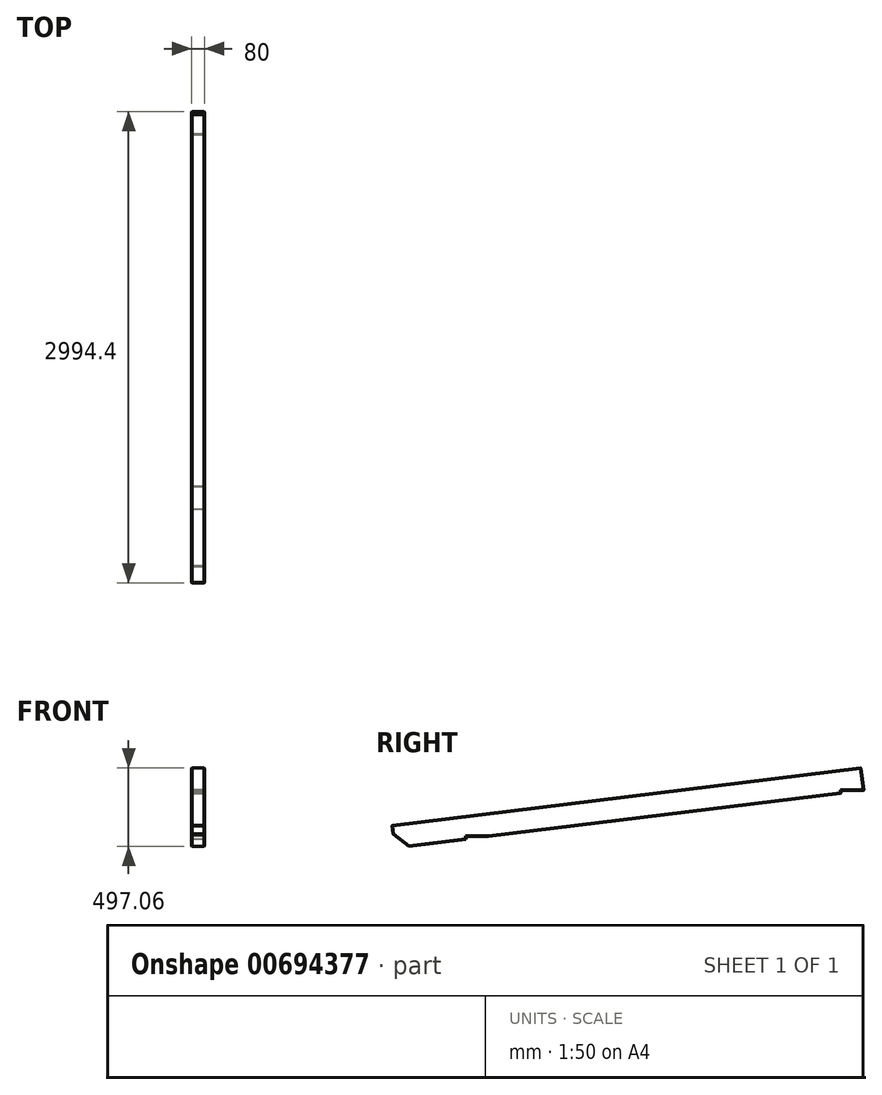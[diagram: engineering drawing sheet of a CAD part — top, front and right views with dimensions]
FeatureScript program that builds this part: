
annotation { "Feature Type Name" : "Feature", "Feature Type Description" : "" }
export const myFeature = defineFeature(function(context is Context, id is Id, definition is map)
    precondition{}
    {
        {
            var Q0;
            Q0=qCreatedBy(makeId("Right.planeOp"),FACE);
            var sketch = newSketch(context, id + "F0", { "sketchPlane" : qUnion([Q0])});
            skLineSegment(sketch, "E0.trimOffspring", {"start": v(2426.65, 153.57) * mm, "end": v(2426.66, 153.57) * mm, "construction": true});
            skLineSegment(sketch, "E1.right", {"start": v(44.48, -138.84) * mm, "end": v(44.48, -138.92) * mm, "construction": true});
            skLineSegment(sketch, "E2", {"start": v(-568.53, -69.1) * mm, "end": v(-561.93, -122.85) * mm});
            skLineSegment(sketch, "E3", {"start": v(-561.93, -122.85) * mm, "end": v(-461.8, -201.08) * mm});
            skLineSegment(sketch, "E4", {"start": v(-461.8, -201.08) * mm, "end": v(-99.52, -156.6) * mm});
            skLineSegment(sketch, "E5", {"start": v(-99.52, -156.6) * mm, "end": v(-99.52, -138.84) * mm});
            skLineSegment(sketch, "E6", {"start": v(-99.52, -138.84) * mm, "end": v(44.48, -138.84) * mm});
            skLineSegment(sketch, "E7", {"start": v(44.48, -138.84) * mm, "end": v(2282.47, 135.87) * mm});
            skLineSegment(sketch, "E8", {"start": v(2282.47, 135.87) * mm, "end": v(2282.47, 153.57) * mm});
            skLineSegment(sketch, "E9", {"start": v(2282.47, 153.57) * mm, "end": v(2426.66, 153.57) * mm});
            skLineSegment(sketch, "E10", {"start": v(2426.66, 153.57) * mm, "end": v(2409.1, 296.5) * mm});
            skLineSegment(sketch, "E11", {"start": v(2409.1, 296.5) * mm, "end": v(-568.53, -69.1) * mm});
            skSolve(sketch);
        }
        {
            var Q0;
            Q0=makeQuery(id+"F0.imprint","IMPRINT",FACE,{"disambiguationData":[TD([[makeQuery(id+"F0.imprint","IMPRINT",EDGE,{"derivedFrom":sQuery(id+"F0.wireOp",EDGE,"E2")}),1.0]])]});
            extrude(context, id + "F1", {"entities" : qUnion([Q0]), "depth" : 80 * mm, "offsetDistance" : 25 * mm});
        }
        {
            var Q0;
            Q0=makeQuery(id+"F1.opExtrude","SWEPT_FACE",FACE,{"disambiguationData":[OSD([sQuery(id+"F0.wireOp",EDGE,"E2")])]});
            var Q1;
            Q1=makeQuery(id+"F1.opExtrude","SWEPT_FACE",FACE,{"disambiguationData":[OSD([sQuery(id+"F0.wireOp",EDGE,"E3")])]});
            var Q2;
            Q2=makeQuery(id+"F1.opExtrude","CAP_FACE",FACE,{"disambiguationData":[OSD([sQuery(id+"F0.wireOp",EDGE,"E2"),sQuery(id+"F0.wireOp",EDGE,"E3"),sQuery(id+"F0.wireOp",EDGE,"E4"),sQuery(id+"F0.wireOp",EDGE,"E5"),sQuery(id+"F0.wireOp",EDGE,"E6"),sQuery(id+"F0.wireOp",EDGE,"E7"),sQuery(id+"F0.wireOp",EDGE,"E8"),sQuery(id+"F0.wireOp",EDGE,"E9"),sQuery(id+"F0.wireOp",EDGE,"E10"),sQuery(id+"F0.wireOp",EDGE,"E11")])],"isStart":false});
            var Q3;
            Q3=makeQuery(id+"F1.opExtrude","CAP_EDGE",EDGE,{"disambiguationData":[OSD([sQuery(id+"F0.wireOp",EDGE,"E11")])],"isStart":true});
            var Q4;
            Q4=makeQuery(id+"F1.opExtrude","SWEPT_FACE",FACE,{"disambiguationData":[OSD([sQuery(id+"F0.wireOp",EDGE,"E10")])]});
            var Q5;
            Q5=makeQuery(id+"F1.opExtrude","SWEPT_FACE",FACE,{"disambiguationData":[OSD([sQuery(id+"F0.wireOp",EDGE,"E7")])]});
            var Q6;
            Q6=makeQuery(id+"F1.opExtrude","CAP_FACE",FACE,{"disambiguationData":[OSD([sQuery(id+"F0.wireOp",EDGE,"E2"),sQuery(id+"F0.wireOp",EDGE,"E3"),sQuery(id+"F0.wireOp",EDGE,"E4"),sQuery(id+"F0.wireOp",EDGE,"E5"),sQuery(id+"F0.wireOp",EDGE,"E6"),sQuery(id+"F0.wireOp",EDGE,"E7"),sQuery(id+"F0.wireOp",EDGE,"E8"),sQuery(id+"F0.wireOp",EDGE,"E9"),sQuery(id+"F0.wireOp",EDGE,"E10"),sQuery(id+"F0.wireOp",EDGE,"E11")])],"isStart":true});
            chamfer(context, id + "F2", {"entities" : qUnion([Q0, Q1, Q2, Q3, Q4, Q5, Q6]), "width" : 3 * mm, "tangentPropagation" : true});
        }
    });
